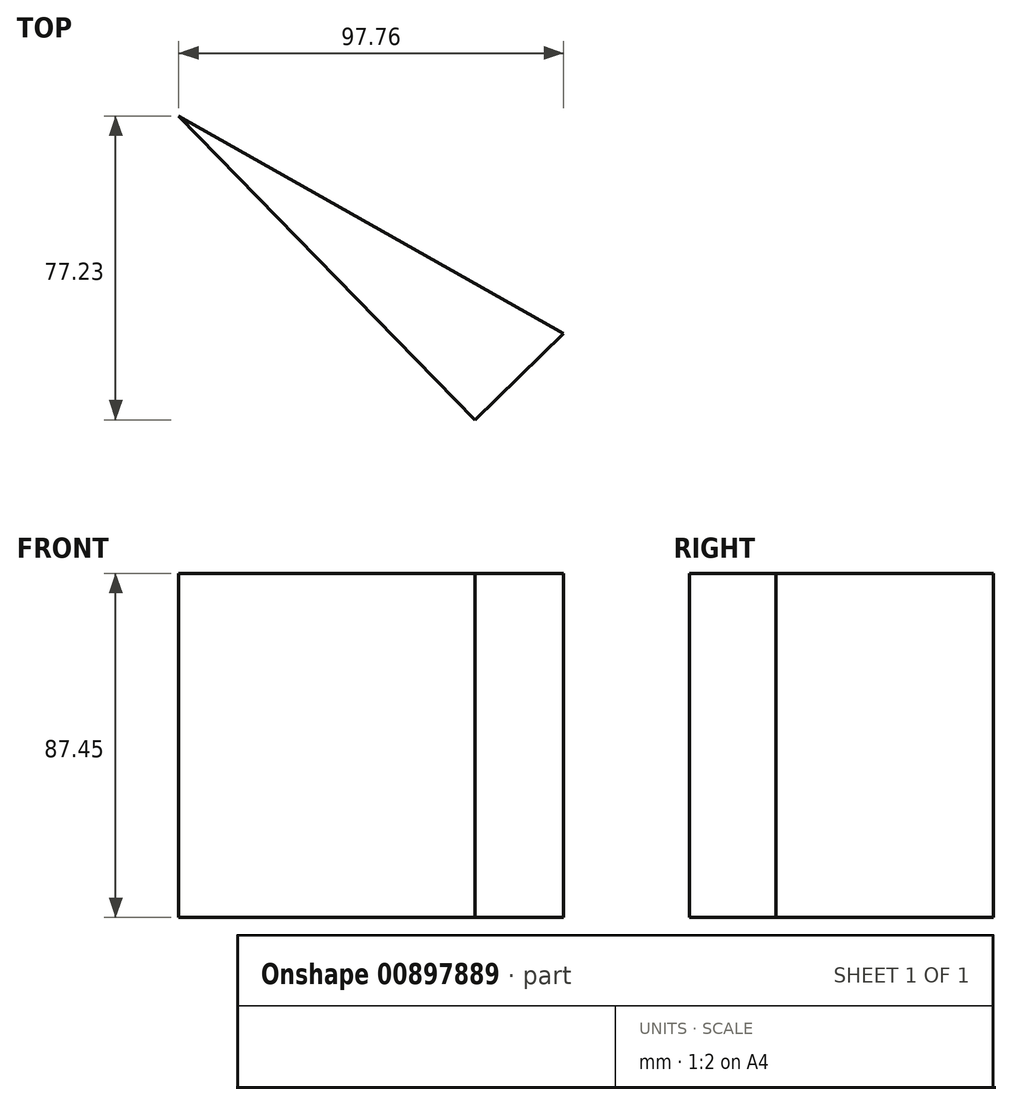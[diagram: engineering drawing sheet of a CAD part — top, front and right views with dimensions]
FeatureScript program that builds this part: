
annotation { "Feature Type Name" : "Feature", "Feature Type Description" : "" }
export const myFeature = defineFeature(function(context is Context, id is Id, definition is map)
    precondition{}
    {
        {
            var Q0;
            Q0=qCreatedBy(makeId("Top.planeOp"),FACE);
            var sketch = newSketch(context, id + "F0", { "sketchPlane" : qUnion([Q0])});
            skLineSegment(sketch, "E0", {"start": v(22.47, 21.9) * mm, "end": v(0, 0) * mm});
            skLineSegment(sketch, "E1", {"start": v(0, 0) * mm, "end": v(-75.29, 77.23) * mm});
            skLineSegment(sketch, "E2", {"start": v(-75.29, 77.23) * mm, "end": v(22.47, 21.9) * mm});
            skSolve(sketch);
        }
        {
            var Q0;
            Q0=makeQuery(id+"F0.imprint","IMPRINT",FACE,{"disambiguationData":[TD([[makeQuery(id+"F0.imprint","IMPRINT",EDGE,{"derivedFrom":sQuery(id+"F0.wireOp",EDGE,"E0")}),-1.0]])]});
            extrude(context, id + "F1", {"entities" : qUnion([Q0]), "oppositeDirection" : true, "depth" : 87.45 * mm, "offsetDistance" : 25.4 * mm});
        }
    });
